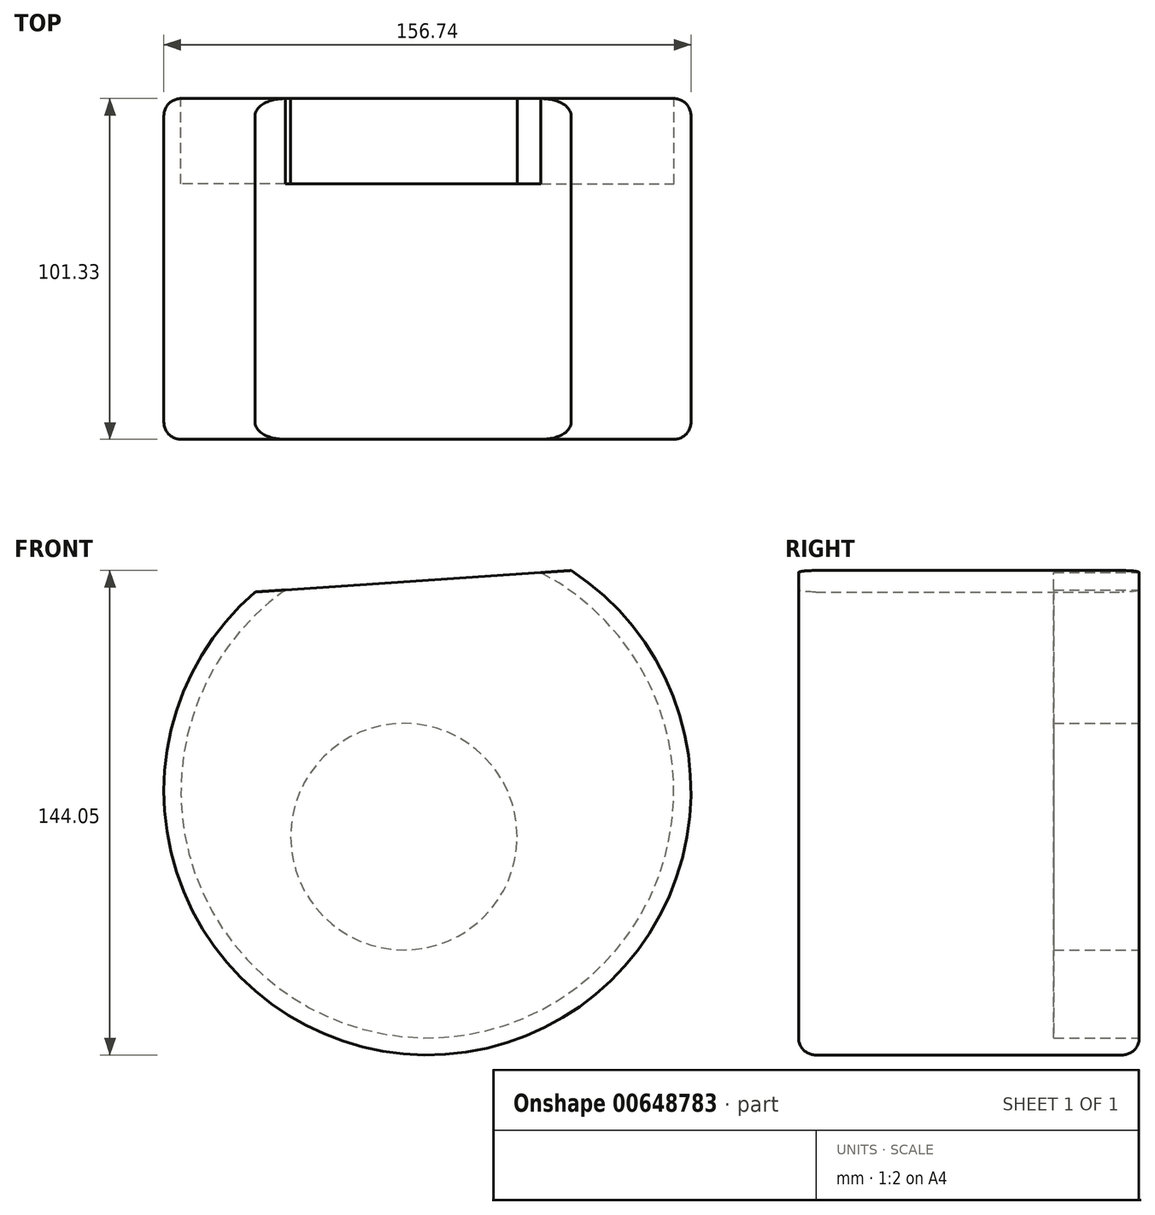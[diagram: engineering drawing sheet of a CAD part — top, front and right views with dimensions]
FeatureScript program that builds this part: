
annotation { "Feature Type Name" : "Feature", "Feature Type Description" : "" }
export const myFeature = defineFeature(function(context is Context, id is Id, definition is map)
    precondition{}
    {
        {
            var Q0;
            Q0=qCreatedBy(makeId("Front.planeOp"),FACE);
            var sketch = newSketch(context, id + "F0", { "sketchPlane" : qUnion([Q0])});
            skArc(sketch, "E0", {"start": v(-61.8, 57.93) * mm, "mid": v(-5.26, -79.55) * mm, "end": v(32.17, 64.32) * mm});
            skLineSegment(sketch, "E1", {"start": v(-61.8, 57.93) * mm, "end": v(32.17, 64.32) * mm});
            skSolve(sketch);
        }
        {
            var Q0;
            Q0 = qSketchRegion(id + "F0", true);
            extrude(context, id + "F1", {"entities" : qUnion([Q0]), "depth" : 101.33 * mm, "offsetDistance" : 25.4 * mm});
        }
        {
            var Q0;
            Q0=makeQuery(id+"F1.opExtrude","CAP_EDGE",EDGE,{"disambiguationData":[OSD([sQuery(id+"F0.wireOp",EDGE,"E0")])],"isStart":false});
            fillet(context, id + "F2", {"entities" : qUnion([Q0]), "radius" : 5.08 * mm, "tangentPropagation" : true, "allowEdgeOverflow" : false});
        }
        {
            var Q0;
            Q0=makeQuery(id+"F1.opExtrude","CAP_EDGE",EDGE,{"disambiguationData":[OSD([sQuery(id+"F0.wireOp",EDGE,"E0")])],"isStart":true});
            fillet(context, id + "F3", {"entities" : qUnion([Q0]), "radius" : 5.08 * mm, "tangentPropagation" : true, "allowEdgeOverflow" : false});
        }
        {
            var Q0;
            Q0=makeQuery(id+"F1.opExtrude","CAP_FACE",FACE,{"disambiguationData":[OSD([sQuery(id+"F0.wireOp",EDGE,"E0"),sQuery(id+"F0.wireOp",EDGE,"E1")])],"isStart":true});
            var sketch = newSketch(context, id + "F4", { "sketchPlane" : qUnion([Q0])});
            skCircle(sketch, "E2", {"center": v(17.55, -14.82) * mm, "radius": 33.67 * mm});
            skSolve(sketch);
        }
        {
            var Q0;
            Q0=makeQuery(id+"F4.imprint","IMPRINT",FACE,{"disambiguationData":[TD([[makeQuery(id+"F4.imprint","IMPRINT",EDGE,{"derivedFrom":sQuery(id+"F4.wireOp",EDGE,"E2")}),-1.0]])]});
            var Q1;
            Q1=sQuery(id+"F4.wireOp",EDGE,"E2");
            extrude(context, id + "F5", {"entities" : qUnion([Q0]), "operationType" : NewBodyOperationType.REMOVE, "surfaceEntities" : qUnion([Q1]), "oppositeDirection" : true, "depth" : 25.4 * mm, "offsetDistance" : 25.4 * mm});
        }
    });
